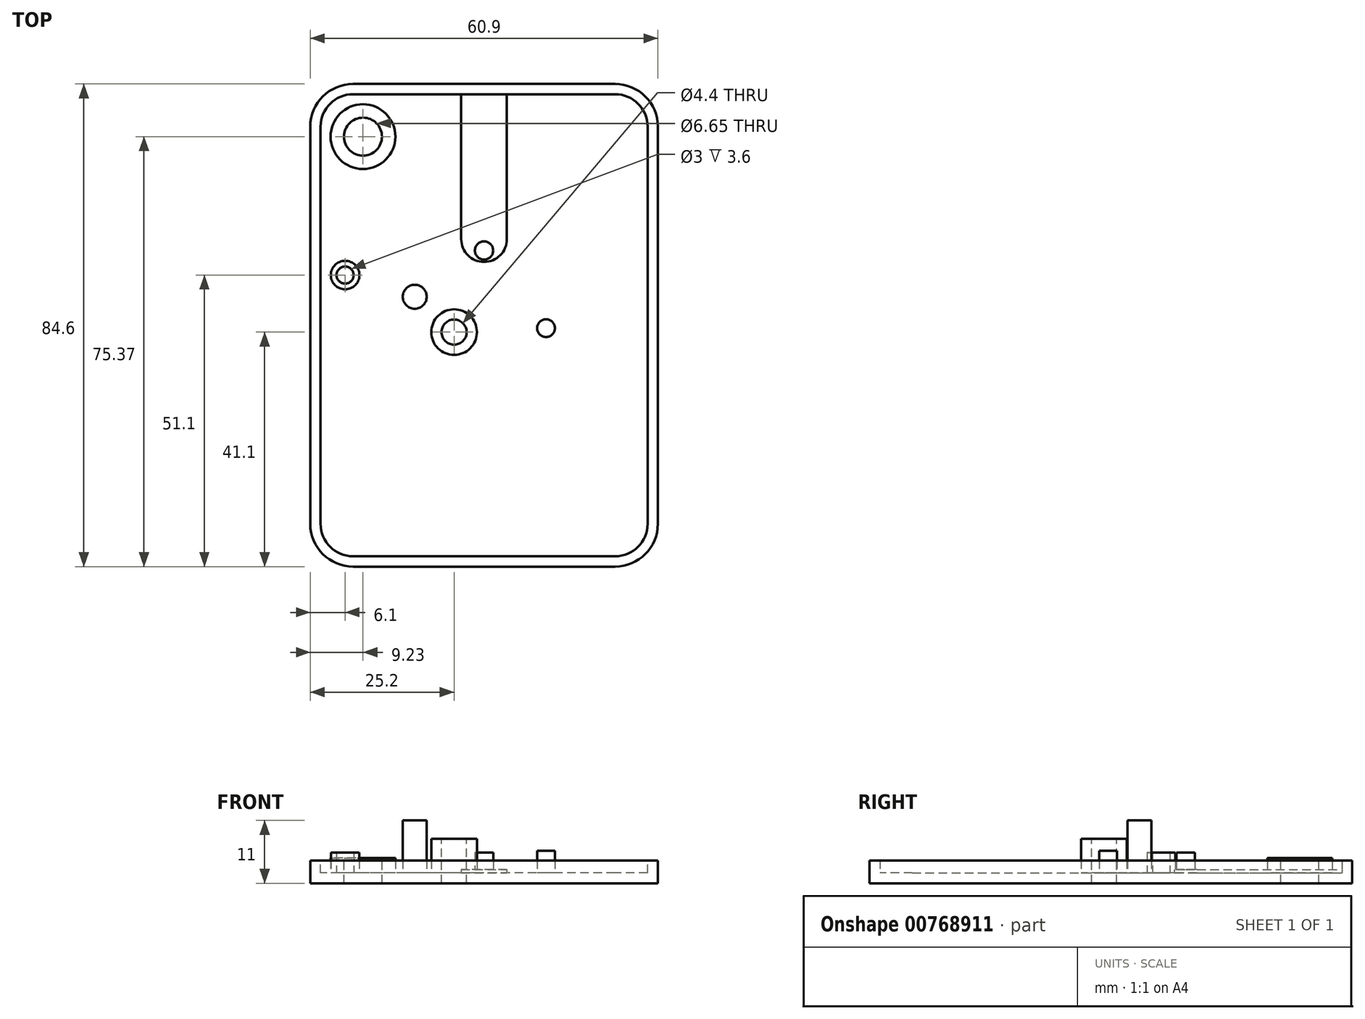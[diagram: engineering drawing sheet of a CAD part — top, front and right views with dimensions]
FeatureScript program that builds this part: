
annotation { "Feature Type Name" : "Feature", "Feature Type Description" : "" }
export const myFeature = defineFeature(function(context is Context, id is Id, definition is map)
    precondition{}
    {
        {
            var Q0;
            Q0=qCreatedBy(makeId("Top.planeOp"),FACE);
            var sketch = newSketch(context, id + "F0", { "sketchPlane" : qUnion([Q0])});
            skLineSegment(sketch, "E0.bottom", {"start": v(22.95, -42.3) * mm, "end": v(-22.95, -42.3) * mm});
            skLineSegment(sketch, "E0.top", {"start": v(22.95, 42.3) * mm, "end": v(-22.95, 42.3) * mm});
            skLineSegment(sketch, "E0.left", {"start": v(30.45, -34.8) * mm, "end": v(30.45, 34.8) * mm});
            skLineSegment(sketch, "E0.right", {"start": v(-30.45, -34.8) * mm, "end": v(-30.45, 34.8) * mm});
            skPoint(sketch, "E0.middle", {"position": v(0, 0) * mm});
            skPoint(sketch, "E1.visualSharp", {"position": v(-30.45, 42.3) * mm});
            skArc(sketch, "E1.filletArc", {"start": v(-22.95, 42.3) * mm, "mid": v(-28.25, 40.1) * mm, "end": v(-30.45, 34.8) * mm});
            skPoint(sketch, "E2.visualSharp", {"position": v(30.45, 42.3) * mm});
            skArc(sketch, "E2.filletArc", {"start": v(30.45, 34.8) * mm, "mid": v(28.25, 40.1) * mm, "end": v(22.95, 42.3) * mm});
            skPoint(sketch, "E3.visualSharp", {"position": v(30.45, -42.3) * mm});
            skArc(sketch, "E3.filletArc", {"start": v(22.95, -42.3) * mm, "mid": v(28.25, -40.1) * mm, "end": v(30.45, -34.8) * mm});
            skPoint(sketch, "E4.visualSharp", {"position": v(-30.45, -42.3) * mm});
            skArc(sketch, "E4.filletArc", {"start": v(-30.45, -34.8) * mm, "mid": v(-28.25, -40.1) * mm, "end": v(-22.95, -42.3) * mm});
            skSolve(sketch);
        }
        {
            var Q0;
            Q0 = qSketchRegion(id + "F0", true);
            extrude(context, id + "F1", {"entities" : qUnion([Q0]), "depth" : 4 * mm, "offsetDistance" : 25 * mm});
        }
        {
            var Q0;
            Q0=makeQuery(id+"F1.opExtrude","CAP_FACE",FACE,{"disambiguationData":[OSD([sQuery(id+"F0.wireOp",EDGE,"E0.bottom"),sQuery(id+"F0.wireOp",EDGE,"E0.top"),sQuery(id+"F0.wireOp",EDGE,"E0.left"),sQuery(id+"F0.wireOp",EDGE,"E0.right"),sQuery(id+"F0.wireOp",EDGE,"E1.filletArc"),sQuery(id+"F0.wireOp",EDGE,"E2.filletArc"),sQuery(id+"F0.wireOp",EDGE,"E3.filletArc"),sQuery(id+"F0.wireOp",EDGE,"E4.filletArc")])],"isStart":false});
            shell(context, id + "F2", {"entities" : qUnion([Q0]), "thickness" : 1.8 * mm});
        }
        {
            var Q0;
            Q0=makeQuery(id+"F2.opShell","OFFSET_FACE",FACE,{"disambiguationData":[OSD([sQuery(id+"F0.wireOp",EDGE,"E0.bottom"),sQuery(id+"F0.wireOp",EDGE,"E0.top"),sQuery(id+"F0.wireOp",EDGE,"E0.left"),sQuery(id+"F0.wireOp",EDGE,"E0.right"),sQuery(id+"F0.wireOp",EDGE,"E1.filletArc"),sQuery(id+"F0.wireOp",EDGE,"E2.filletArc"),sQuery(id+"F0.wireOp",EDGE,"E3.filletArc"),sQuery(id+"F0.wireOp",EDGE,"E4.filletArc")])]});
            var sketch = newSketch(context, id + "F3", { "sketchPlane" : qUnion([Q0])});
            skCircle(sketch, "E5", {"center": v(-21.22, 33.07) * mm, "radius": 3.33 * mm});
            skCircle(sketch, "E6", {"center": v(-21.22, 33.07) * mm, "radius": 5.68 * mm});
            skCircle(sketch, "E7", {"center": v(0, 13.1) * mm, "radius": 1.6 * mm});
            skArc(sketch, "E8", {"start": v(4, 15.1) * mm, "mid": v(0, 11.1) * mm, "end": v(-4, 15.1) * mm});
            skLineSegment(sketch, "E9", {"start": v(0, 13.1) * mm, "end": v(0, 15.1) * mm, "construction": true});
            skLineSegment(sketch, "E10", {"start": v(0, 15.1) * mm, "end": v(-4, 15.1) * mm, "construction": true});
            skLineSegment(sketch, "E11", {"start": v(0, 15.1) * mm, "end": v(4, 15.1) * mm, "construction": true});
            skLineSegment(sketch, "E12", {"start": v(-4, 15.1) * mm, "end": v(-4, 40.5) * mm});
            skLineSegment(sketch, "E13", {"start": v(4, 15.1) * mm, "end": v(4, 40.5) * mm});
            skLineSegment(sketch, "E14", {"start": v(0, 13.1) * mm, "end": v(0, 0) * mm, "construction": true});
            skCircle(sketch, "E15", {"center": v(-24.35, 8.8) * mm, "radius": 1.5 * mm});
            skCircle(sketch, "E16", {"center": v(-24.35, 8.8) * mm, "radius": 2.5 * mm});
            skCircle(sketch, "E17", {"center": v(-12.15, 5) * mm, "radius": 2.1 * mm});
            skCircle(sketch, "E18", {"center": v(-5.25, -1.2) * mm, "radius": 2.2 * mm});
            skCircle(sketch, "E19", {"center": v(-5.25, -1.2) * mm, "radius": 4 * mm});
            skCircle(sketch, "E20", {"center": v(10.85, -0.5) * mm, "radius": 1.55 * mm});
            skSolve(sketch);
        }
        {
            var Q0;
            Q0=makeQuery(id+"F3.imprint","IMPRINT",FACE,{"disambiguationData":[TD([[makeQuery(id+"F3.imprint","IMPRINT",EDGE,{"derivedFrom":sQuery(id+"F3.wireOp",EDGE,"E5")}),1.0]])]});
            var Q1;
            Q1=makeQuery(id+"F3.imprint","IMPRINT",FACE,{"disambiguationData":[TD([[makeQuery(id+"F3.imprint","IMPRINT",EDGE,{"derivedFrom":sQuery(id+"F3.wireOp",EDGE,"E18")}),1.0]])]});
            extrude(context, id + "F4", {"entities" : qUnion([Q0, Q1]), "operationType" : NewBodyOperationType.REMOVE, "endBound" : BoundingType.THROUGH_ALL, "oppositeDirection" : true, "depth" : 25 * mm, "offsetDistance" : 25 * mm});
        }
        {
            var Q0;
            Q0=makeQuery(id+"F3.imprint","IMPRINT",FACE,{"disambiguationData":[TD([[makeQuery(id+"F3.imprint","IMPRINT",EDGE,{"derivedFrom":sQuery(id+"F3.wireOp",EDGE,"E7")}),-1.0]])]});
            extrude(context, id + "F5", {"entities" : qUnion([Q0]), "operationType" : NewBodyOperationType.ADD, "depth" : 0.6 * mm, "offsetDistance" : 25 * mm});
        }
        {
            var Q0;
            Q0=makeQuery(id+"F3.imprint","IMPRINT",FACE,{"disambiguationData":[TD([[makeQuery(id+"F3.imprint","IMPRINT",EDGE,{"derivedFrom":sQuery(id+"F3.wireOp",EDGE,"E5")}),-1.0]])]});
            extrude(context, id + "F6", {"entities" : qUnion([Q0]), "operationType" : NewBodyOperationType.ADD, "depth" : 2.6 * mm, "offsetDistance" : 25 * mm});
        }
        {
            var Q0;
            Q0=makeQuery(id+"F3.imprint","IMPRINT",FACE,{"disambiguationData":[TD([[makeQuery(id+"F3.imprint","IMPRINT",EDGE,{"derivedFrom":sQuery(id+"F3.wireOp",EDGE,"E7")}),1.0]])]});
            var Q1;
            Q1=makeQuery(id+"F3.imprint","IMPRINT",FACE,{"disambiguationData":[TD([[makeQuery(id+"F3.imprint","IMPRINT",EDGE,{"derivedFrom":sQuery(id+"F3.wireOp",EDGE,"E15")}),-1.0]])]});
            extrude(context, id + "F7", {"entities" : qUnion([Q0, Q1]), "operationType" : NewBodyOperationType.ADD, "depth" : 3.6 * mm, "offsetDistance" : 25 * mm});
        }
        {
            var Q0;
            Q0=makeQuery(id+"F3.imprint","IMPRINT",FACE,{"disambiguationData":[TD([[makeQuery(id+"F3.imprint","IMPRINT",EDGE,{"derivedFrom":sQuery(id+"F3.wireOp",EDGE,"E20")}),1.0]])]});
            extrude(context, id + "F8", {"entities" : qUnion([Q0]), "operationType" : NewBodyOperationType.ADD, "depth" : 3.9 * mm, "offsetDistance" : 25 * mm});
        }
        {
            var Q0;
            Q0=makeQuery(id+"F3.imprint","IMPRINT",FACE,{"disambiguationData":[TD([[makeQuery(id+"F3.imprint","IMPRINT",EDGE,{"derivedFrom":sQuery(id+"F3.wireOp",EDGE,"E18")}),-1.0]])]});
            extrude(context, id + "F9", {"entities" : qUnion([Q0]), "operationType" : NewBodyOperationType.ADD, "depth" : 6 * mm, "offsetDistance" : 25 * mm});
        }
        {
            var Q0;
            Q0=makeQuery(id+"F3.imprint","IMPRINT",FACE,{"disambiguationData":[TD([[makeQuery(id+"F3.imprint","IMPRINT",EDGE,{"derivedFrom":sQuery(id+"F3.wireOp",EDGE,"E17")}),1.0]])]});
            extrude(context, id + "F10", {"entities" : qUnion([Q0]), "operationType" : NewBodyOperationType.ADD, "depth" : 9.2 * mm, "offsetDistance" : 25 * mm});
        }
    });
